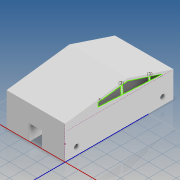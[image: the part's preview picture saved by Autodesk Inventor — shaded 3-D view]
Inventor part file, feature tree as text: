
AUTODESK INVENTOR PART (.ipt)
format: ipt  version: 2020 (Build 240168000, 168)  size: 276,992 bytes
history: native  units: mm
features: extrude x8, sketch x7
ambient origin geometry x8: Origin, YZ Plane, XZ Plane, XY Plane, X Axis, Y Axis, Z Axis, Center Point
bodies: Solid1 (feature_tree)
feature tree (15):
  extrude  "Extrusion1"  Depth=156.0mm
  extrude  "Extrusion2"  Depth=3.0mm
  extrude  "Extrusion12"  Depth=3.0mm
  extrude  "Extrusion13"  Depth=3.0mm
  extrude  "Extrusion14"  Depth=3.0mm
  extrude  "Extrusion15"  Depth=12.0mm TaperAngle=0.0deg
  sketch  "Sketch19"  dims[d96=81.0mm d97=0.0mm d123=3.0mm d124=0.0mm d125=10.0mm d150=22.5mm d151=0.0mm d152=16.0mm d153=11.2mm d154=16.0mm d155=11.2mm d156=6.0mm d157=6.0mm d158=104.25mm d159=0.0mm d160=50.0mm d161=3.0mm d162=50.0mm d163=3.0mm d164=35.0mm d165=0.0mm d176=90.0deg d178=3.0mm d180=3.0mm d182=3.0mm d183=3.0mm d184=5.0mm d187=0.2mm d188=0.0mm d189=0.1mm d190=84.1mm d191=0.0mm d192=0.0mm d193=0.5mm d194=0.872665mm d195=0.5mm d196=0.872665mm]
  extrude  "Extrusion17"  Depth=3.0mm TaperAngle=0.0deg
  extrude  "Extrusion18"  Depth=10.0mm
  sketch  "Sketch1"  dims[d0=84.0mm d1=156.0mm]
  sketch  "Sketch2"  dims[d2=3.0mm d3=3.0mm]
  sketch  "Sketch15"  dims[d4=3.0mm d5=3.0mm]
  sketch  "Sketch16"  dims[d6=15.0mm d7=0.0mm d8=3.0mm]
  sketch  "Sketch17"  dims[d9=3.0mm d10=3.0mm]
  sketch  "Sketch18"  dims[d11=3.0mm d12=12.0mm d13=0.0mm]
